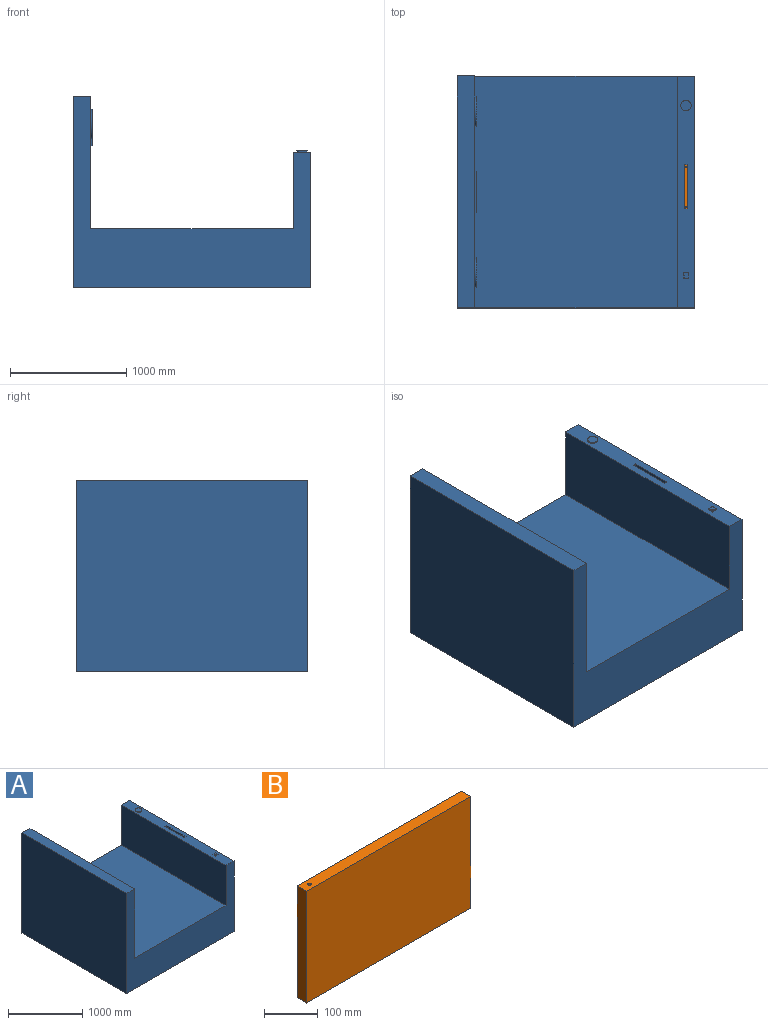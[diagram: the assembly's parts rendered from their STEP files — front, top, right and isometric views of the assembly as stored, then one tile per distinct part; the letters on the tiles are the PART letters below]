
ASSEMBLY  parts=2 mates=1
PART A: 40 faces, bbox 2044.7x1993.9x1651 mm
  f0: plane 51.19x50.8mm, normal (0,0,1), area 2525.3mm2, adj f27,f28,f29,f30,f31,f32,f33,f34
  f1: plane 1993.9x1739.9mm, normal (0,0,1), area 3469186.6mm2, adj f2,f7,f8,f21
  f2: plane 1993.9x1143mm, normal (1,0,0), area 2067680.4mm2, adj f1,f3,f7,f8,f9,f11,f13,f14
  f3: plane 1993.9x152.4mm, normal (0,0,1), area 303870.4mm2, adj f2,f4,f7,f8
  f4: plane 1993.9x1651mm, normal (-1,0,0), area 3291928.9mm2, adj f3,f5,f7,f8
  f5: plane 2044.7x1993.9mm, normal (0,0,-1), area 4076927.3mm2, adj f4,f6,f7,f8
  f6: plane 1993.9x1168.4mm, normal (1,0,0), area 2329672.8mm2, adj f5,f7,f8,f23
  f7: plane 2044.7x1651mm, normal (0,-1,0), area 1313545.8mm2, adj f1,f2,f3,f4,f5,f6,f21,f23
  f8: plane 2044.7x1651mm, normal (0,1,0), area 1313545.8mm2, adj f1,f2,f3,f4,f5,f6,f21,f23
  f9: cylinder r=127mm len=254mm, axis (-1,0,0), area 8107.3mm2, adj f2,f10
  f10: plane 254x254mm, normal (1,0,0), area 50670.7mm2, adj f9
  f11: cylinder r=127mm len=254mm, axis (-1,0,0), area 8107.3mm2, adj f2,f12
  f12: plane 254x254mm, normal (1,0,0), area 50670.7mm2, adj f11
  f13: plane 355.6x10.16mm, normal (0,0,-1), area 3612.9mm2, adj f2,f14,f16,f17
  f14: plane 309.35x10.16mm, normal (0,1,0), area 3143mm2, adj f2,f13,f15,f17
  f15: plane 355.6x10.16mm, normal (0,0,1), area 3612.9mm2, adj f2,f14,f16,f17
  f16: plane 309.35x10.16mm, normal (0,-1,0), area 3143mm2, adj f2,f13,f15,f17
  f17: plane 355.6x309.35mm, normal (1,0,0), area 110005.8mm2, adj f13,f14,f15,f16
  f18: plane 660.4x25.4mm, normal (0,1,0), area 16774.2mm2, adj f19,f22,f23,f24
  f19: plane 660.4x381mm, normal (1,0,0), area 251612.4mm2, adj f18,f20,f23,f24
  f20: plane 660.4x25.4mm, normal (0,-1,0), area 16774.2mm2, adj f19,f22,f23,f24
  f21: plane 1993.9x660.4mm, normal (-1,0,0), area 1316771.6mm2, adj f1,f7,f8,f23
  f22: plane 660.4x381mm, normal (-1,0,0), area 251612.4mm2, adj f18,f20,f23,f24
  f23: plane 1993.9x152.4mm, normal (0,0,1), area 285395.3mm2, adj f6,f7,f8,f18,f19,f20,f21,f22
  f24: plane 381x25.4mm, normal (0,0,1), area 9614.1mm2, adj f18,f19,f20,f22,f36,f38
  f25: cylinder r=44.45mm len=88.9mm, axis (0,0,-1), area 2837.6mm2, adj f23,f26
  f26: plane 88.9x88.9mm, normal (0,0,1), area 6207.2mm2, adj f25
  f27: plane 50.8x10.16mm, normal (0,-1,0), area 516.1mm2, adj f0,f23,f28,f30
  f28: plane 50.8x10.16mm, normal (1,-0.01,0), area 516.1mm2, adj f0,f23,f27,f29
  f29: plane 51.19x10.16mm, normal (0,1,0), area 520.1mm2, adj f0,f23,f28,f30
  f30: plane 50.8x10.16mm, normal (-1,0,0), area 516.1mm2, adj f0,f23,f27,f29
  f31: plane 5.08x2.54mm, normal (0,-1,0), area 12.9mm2, adj f0,f32,f34,f35
  f32: plane 12.7x2.54mm, normal (1,-0.01,0), area 32.3mm2, adj f0,f31,f33,f35
  f33: plane 5.18x2.54mm, normal (0,1,0), area 13.2mm2, adj f0,f32,f34,f35
  f34: plane 12.7x2.54mm, normal (-1,0,0), area 32.3mm2, adj f0,f31,f33,f35
  f35: plane 12.7x5.18mm, normal (0,0,1), area 65.2mm2, adj f31,f32,f33,f34
  f36: cylinder r=3.17mm len=25.4mm, axis (0,0,-1), area 506.7mm2, adj f24,f37
  f37: plane 6.35x6.35mm, normal (0,0,1), area 31.7mm2, adj f36
  f38: cylinder r=3.17mm len=25.4mm, axis (0,0,-1), area 506.7mm2, adj f24,f39
  f39: plane 6.35x6.35mm, normal (0,0,1), area 31.7mm2, adj f38
PART B: 7 faces, bbox 431.8x25.4x254 mm
  f0: plane 254x25.4mm, normal (-1,0,0), area 6451.6mm2, adj f1,f3,f4,f5
  f1: plane 431.8x25.4mm, normal (0,0,-1), area 10931.9mm2, adj f0,f2,f4,f5,f6
  f2: plane 254x25.4mm, normal (1,0,0), area 6451.6mm2, adj f1,f3,f4,f5
  f3: plane 431.8x25.4mm, normal (0,0,1), area 10931.9mm2, adj f0,f2,f4,f5,f6
  f4: plane 431.8x254mm, normal (0,-1,0), area 109677.2mm2, adj f0,f1,f2,f3
  f5: plane 431.8x254mm, normal (0,1,0), area 109677.2mm2, adj f0,f1,f2,f3
  f6: cylinder r=3.38mm len=254mm, axis (0,0,-1), area 5391.4mm2, adj f1,f3
PLACE A at identity fixed
PLACE B rot(axis=(0,0,-1),90deg) t=(959.53,-785.6,-121.13)mm
MATE fastened B.f6 <-> A.f36  axis (0,0,1) through (946.83,-782.32,0.22)mm
